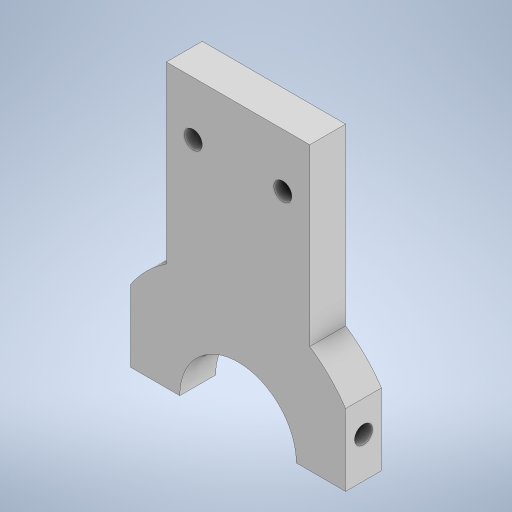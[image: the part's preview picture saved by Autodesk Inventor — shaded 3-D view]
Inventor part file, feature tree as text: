
AUTODESK INVENTOR PART (.ipt)
format: ipt  version: 2023 (Build 270158000, 158)  size: 254,464 bytes
history: native  units: in
note: dims shown in document units (in); Inventor stores cm internally (conversion verified against a paired STEP export)
features: extrude x2, sketch x2
ambient origin geometry x8: Origin, YZ Plane, XZ Plane, XY Plane, X Axis, Y Axis, Z Axis, Center Point
bodies: Body1 (feature_tree)
feature tree (4):
  extrude  "Extrusion3"  Depth=0.25in
  extrude  "Extrusion4"  Depth=1.625in
  sketch  "Sketch1"  dims[d2=0.25in d3=0.25in]
  sketch  "Sketch2"  dims[d6=3.938in d7=1.625in d18=0.75in d19=0.75in d20=1.0in d21=1.0in d22=0.5in d23=0.0in d24=0.563in d25=0.25in d26=4.9375in d27=0.0in d14=0.5in d15=0.0344in d16=0.5in d17=0.0344in]
